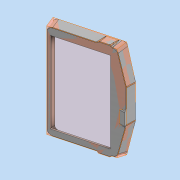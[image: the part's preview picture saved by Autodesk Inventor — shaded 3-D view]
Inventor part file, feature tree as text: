
AUTODESK INVENTOR PART (.ipt)
format: ipt  version: 2022 (Build 260153070, 153G)  size: 1,026,560 bytes
history: native  units: mm
features: other x30, surface_op x15, plane x9, fillet x4, sketch x3, extrude x2, loft x2, mirror x1, thicken_offset x1, split x1
ambient origin geometry x8: Origin, YZ Plane, XZ Plane, XY Plane, X Axis, Y Axis, Z Axis, Center Point
bodies: Body1 (feature_tree), Body2 (feature_tree), Body3 (feature_tree), Body4 (feature_tree), Body5 (feature_tree), Body6 (feature_tree), Body7 (feature_tree), Body8 (feature_tree), Body9 (feature_tree), Body10 (feature_tree), Body11 (feature_tree)
feature tree (68):
  other  "P00173-09-002.ipt"
  other  "Blocks"
  other  "Top_Housing_2"
  other  "Top_Housing_3"
  other  "Top_Housing_4"
  plane  "Work Plane10"
  plane  "Work Plane14"
  plane  "Work Plane26"
  sketch  "Sketch45"  dims[d48=0.0mm d49=90.0deg]
  other  "Front_Cover_Mount"
  fillet  "Fillet13"  Radius=10.0mm
  surface_op  "Extend5"
  surface_op  "Trim12"
  surface_op  "Trim13"
  surface_op  "Trim14"
  surface_op  "Trim15"
  plane  "Work Plane27"
  sketch  "Sketch53"  dims[d159=0.349066mm d160=3.5mm d161=1.5mm d162=3.5mm d163=16.580628mm d165=3.5mm d166=2.0mm d167=28.0mm d168=55.0mm d169=0.349066mm d170=0.349066mm d171=0.2mm d55=2.5mm d92=5.0mm d97=5.0mm]
  plane  "Work Plane28"
  surface_op  "Trim17"
  surface_op  "Trim18"
  surface_op  "Stitch Surface10"
  mirror  "Mirror5"
  surface_op  "Stitch Surface12"
  surface_op  "Stitch Surface13"
  surface_op  "Trim16"
  surface_op  "Stitch Surface14"
  fillet  "Fillet18"  [1 undecoded]
  surface_op  "Extend6"
  thicken_offset  "Thicken9"
  extrude  "Extrusion33"  Depth=2.5mm
  split  "Split8"
  fillet  "Fillet19"  Radius=5.0mm
  fillet  "Fillet21"  Radius=5.0mm
  other  "Side"
  other  "Bottom"
  plane  "Work Plane1"
  other  "Top_Housing"
  other  "Screen_Hole"
  other  "Top_Housing_Bottom_Edge"
  other  "Srf7"
  other  "Mount_Post"
  plane  "Work Plane - TH_Bottom_Edge"
  plane  "Work Plane7"
  plane  "Work Plane - Screen_Top"
  other  "Camera_Top"
  other  "USB_Side"
  other  "Srf21"
  other  "Cover_Mount_Hole"
  other  "Cover_Mount"
  other  "Srf26"
  other  "Srf27"
  other  "Srf30"
  other  "Srf31"
  other  "Srf32"
  other  "Srf33"
  other  "Srf34"
  sketch  "Sketch54"  dims[d186=2.0mm d187=2.0mm d188=24.0mm d189=25.0mm d194=9.5mm d201=21.0mm d202=2.0mm d203=12.5mm d204=2.1mm d197=0.2mm d243=35.0mm d245=3.0mm d246=24.43461mm d247=24.75mm d248=0.0mm d250=4.0mm d253=15.882496mm d254=15.882496mm d257=12.0mm d268=2.0mm d278=3.0mm d284=7.0mm d293=3.0mm d294=2.0mm d295=3.0mm d296=45.0deg d297=45.0deg d298=0.0mm d299=90.0deg d300=0.0mm d301=90.0deg d305=10.0mm d306=10.0mm d311=3.0mm d312=2.0mm d313=22.75mm d314=0.0mm d317=5.0mm d318=3.0mm d320=1.0mm d321=30.0mm d322=1.0mm d323=0.0mm d324=90.0deg d325=0.0mm d326=90.0deg d73=0.5mm d74=0.872665mm d75=0.5mm d76=0.872665mm]
  other  "Srf35"
  extrude  "ExtrusionSrf4"  Depth=2.0mm
  other  "Sides"
  loft  "LoftSrf7"
  loft  "LoftSrf8"
  other  "Block2:1"
  other  "Block2:2"
  other  "Camera_Top:1"
  surface_op  "Stitch Surface11"
  surface_op  "Boundary Patch7"
note: 1 required parameter value undecoded (feature->parameter linkage not recoverable at this tier; creation-order binding heuristic only, values carry confidence <= 0.55)
